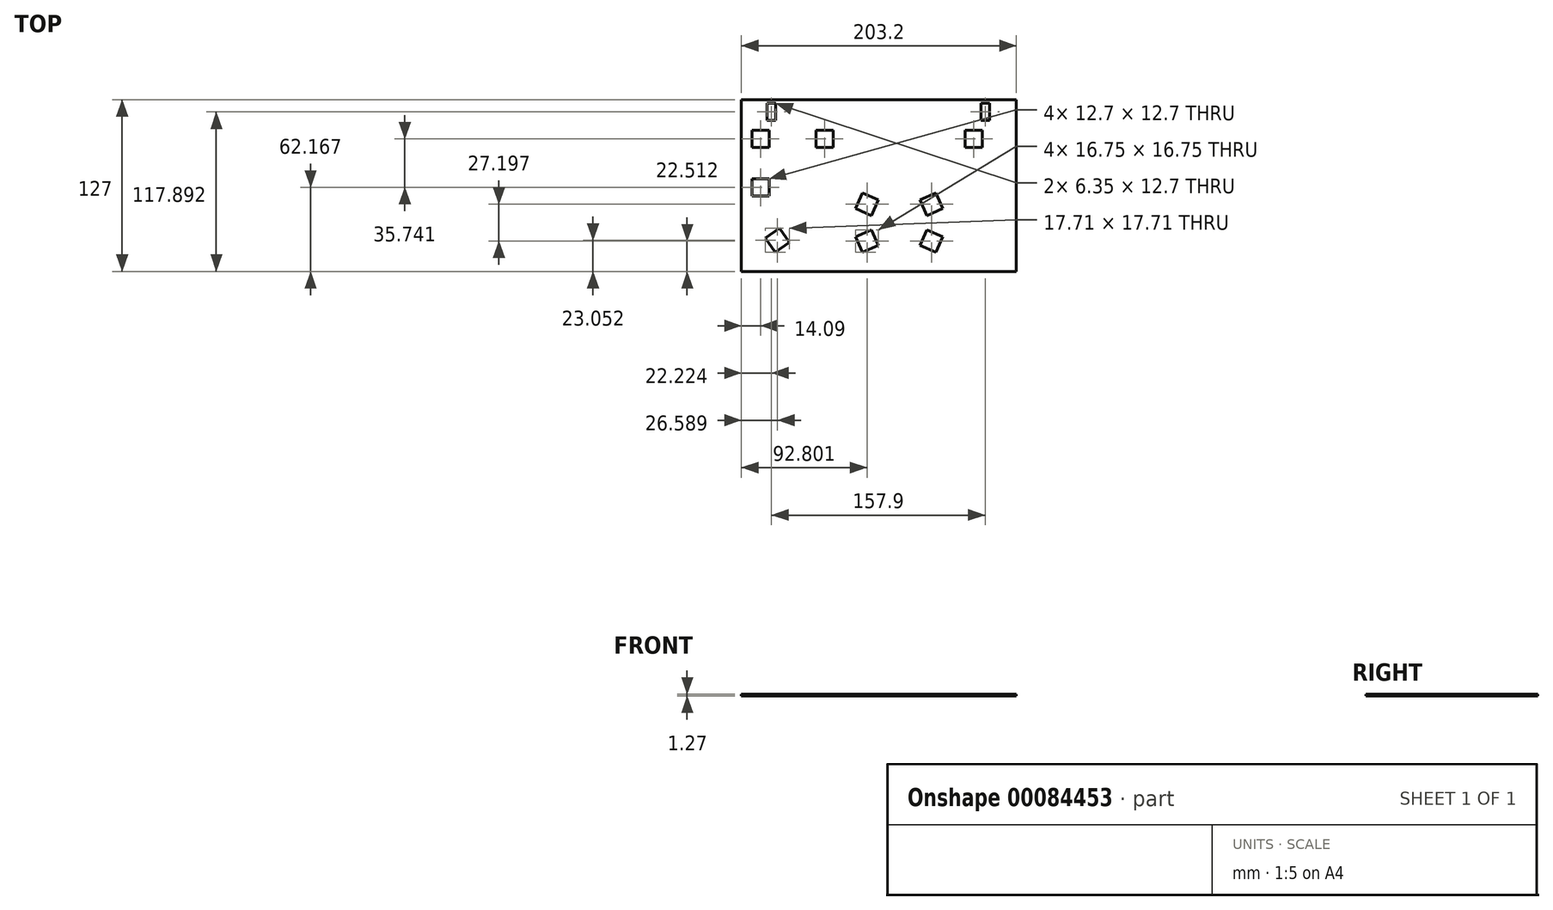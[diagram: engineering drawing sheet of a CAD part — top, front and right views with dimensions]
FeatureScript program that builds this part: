
annotation { "Feature Type Name" : "Feature", "Feature Type Description" : "" }
export const myFeature = defineFeature(function(context is Context, id is Id, definition is map)
    precondition{}
    {
        {
            var Q0;
            Q0=qCreatedBy(makeId("Top.planeOp"),FACE);
            var sketch = newSketch(context, id + "F0", { "sketchPlane" : qUnion([Q0])});
            skLineSegment(sketch, "E0.bottom", {"start": v(-146.8, -36.11) * mm, "end": v(56.4, -36.11) * mm});
            skLineSegment(sketch, "E0.top", {"start": v(-146.8, 90.89) * mm, "end": v(56.4, 90.89) * mm});
            skLineSegment(sketch, "E0.left", {"start": v(-146.8, -36.11) * mm, "end": v(-146.8, 90.89) * mm});
            skLineSegment(sketch, "E0.right", {"start": v(56.4, -36.11) * mm, "end": v(56.4, 90.89) * mm});
            skLineSegment(sketch, "E1.bottom", {"start": v(-139.06, 68.15) * mm, "end": v(-126.36, 68.15) * mm});
            skLineSegment(sketch, "E1.top", {"start": v(-139.06, 55.45) * mm, "end": v(-126.36, 55.45) * mm});
            skLineSegment(sketch, "E1.left", {"start": v(-139.06, 68.15) * mm, "end": v(-139.06, 55.45) * mm});
            skLineSegment(sketch, "E1.right", {"start": v(-126.36, 68.15) * mm, "end": v(-126.36, 55.45) * mm});
            skLineSegment(sketch, "E2.MirrorCS", {"start": v(-139.06, 32.4) * mm, "end": v(-126.36, 32.4) * mm});
            skLineSegment(sketch, "E3.MirrorCS", {"start": v(-139.06, 19.7) * mm, "end": v(-126.36, 19.7) * mm});
            skLineSegment(sketch, "E4.MirrorCS", {"start": v(-126.36, 19.7) * mm, "end": v(-126.36, 32.4) * mm});
            skLineSegment(sketch, "E5.MirrorCS", {"start": v(-139.06, 19.7) * mm, "end": v(-139.06, 32.4) * mm});
            skLineSegment(sketch, "E6.MirrorCS", {"start": v(-129.07, -11.57) * mm, "end": v(-118.72, -4.2) * mm});
            skLineSegment(sketch, "E7.MirrorCS", {"start": v(-118.72, -4.2) * mm, "end": v(-111.36, -14.55) * mm});
            skLineSegment(sketch, "E8.MirrorCS", {"start": v(-129.07, -11.57) * mm, "end": v(-121.7, -21.91) * mm});
            skLineSegment(sketch, "E9.MirrorCS", {"start": v(-121.7, -21.91) * mm, "end": v(-111.36, -14.55) * mm});
            skLineSegment(sketch, "E10.MirrorCS", {"start": v(-79.06, 55.45) * mm, "end": v(-91.76, 55.45) * mm});
            skLineSegment(sketch, "E11.MirrorCS", {"start": v(-91.76, 68.15) * mm, "end": v(-91.76, 55.45) * mm});
            skLineSegment(sketch, "E12.MirrorCS", {"start": v(-79.06, 68.15) * mm, "end": v(-91.76, 68.15) * mm});
            skLineSegment(sketch, "E13.MirrorCS", {"start": v(-79.06, 68.15) * mm, "end": v(-79.06, 55.45) * mm});
            skLineSegment(sketch, "E14.MirrorCS", {"start": v(-45.63, 16.84) * mm, "end": v(-57.24, 21.97) * mm});
            skLineSegment(sketch, "E15.MirrorCS", {"start": v(-45.63, 16.84) * mm, "end": v(-50.76, 5.22) * mm});
            skLineSegment(sketch, "E16.MirrorCS", {"start": v(-50.76, 5.22) * mm, "end": v(-62.37, 10.35) * mm});
            skLineSegment(sketch, "E17.MirrorCS", {"start": v(-57.24, 21.97) * mm, "end": v(-62.37, 10.35) * mm});
            skLineSegment(sketch, "E18.MirrorCS", {"start": v(-45.63, -16.84) * mm, "end": v(-50.76, -5.22) * mm});
            skLineSegment(sketch, "E19.MirrorCS", {"start": v(-57.24, -21.97) * mm, "end": v(-62.37, -10.35) * mm});
            skLineSegment(sketch, "E20.MirrorCS", {"start": v(-50.76, -5.22) * mm, "end": v(-62.37, -10.35) * mm});
            skLineSegment(sketch, "E21.MirrorCS", {"start": v(-45.63, -16.84) * mm, "end": v(-57.24, -21.97) * mm});
            skLineSegment(sketch, "E22.MirrorCS", {"start": v(-14.8, 16.84) * mm, "end": v(-9.67, 5.22) * mm});
            skLineSegment(sketch, "E23.MirrorCS", {"start": v(-9.67, 5.22) * mm, "end": v(1.95, 10.35) * mm});
            skLineSegment(sketch, "E24.MirrorCS", {"start": v(-3.18, 21.97) * mm, "end": v(1.95, 10.35) * mm});
            skLineSegment(sketch, "E25.MirrorCS", {"start": v(-14.8, 16.84) * mm, "end": v(-3.18, 21.97) * mm});
            skLineSegment(sketch, "E26.MirrorCS", {"start": v(-14.8, -16.84) * mm, "end": v(-9.67, -5.22) * mm});
            skLineSegment(sketch, "E27.MirrorCS", {"start": v(-14.8, -16.84) * mm, "end": v(-3.18, -21.97) * mm});
            skLineSegment(sketch, "E28.MirrorCS", {"start": v(-9.67, -5.22) * mm, "end": v(1.95, -10.35) * mm});
            skLineSegment(sketch, "E29.MirrorCS", {"start": v(-3.18, -21.97) * mm, "end": v(1.95, -10.35) * mm});
            skLineSegment(sketch, "E30.MirrorCS", {"start": v(18.63, 68.15) * mm, "end": v(18.63, 55.45) * mm});
            skLineSegment(sketch, "E31.MirrorCS", {"start": v(18.63, 68.15) * mm, "end": v(31.33, 68.15) * mm});
            skLineSegment(sketch, "E32.MirrorCS", {"start": v(31.33, 68.15) * mm, "end": v(31.33, 55.45) * mm});
            skLineSegment(sketch, "E33.MirrorCS", {"start": v(18.63, 55.45) * mm, "end": v(31.33, 55.45) * mm});
            skLineSegment(sketch, "E34.bottom", {"start": v(-127.75, 75.43) * mm, "end": v(-121.4, 75.43) * mm});
            skLineSegment(sketch, "E34.top", {"start": v(-127.75, 88.13) * mm, "end": v(-121.4, 88.13) * mm});
            skLineSegment(sketch, "E34.left", {"start": v(-127.75, 75.43) * mm, "end": v(-127.75, 88.13) * mm});
            skLineSegment(sketch, "E34.right", {"start": v(-121.4, 75.43) * mm, "end": v(-121.4, 88.13) * mm});
            skPoint(sketch, "E35.startSnap0", {"position": v(-45.2, 90.89) * mm});
            skPoint(sketch, "E35.endSnap0", {"position": v(-45.2, -36.11) * mm});
            skLineSegment(sketch, "E36.MirrorCS", {"start": v(36.5, 75.43) * mm, "end": v(36.5, 88.13) * mm});
            skLineSegment(sketch, "E37.MirrorCS", {"start": v(36.5, 88.13) * mm, "end": v(30.15, 88.13) * mm});
            skLineSegment(sketch, "E38.MirrorCS", {"start": v(30.15, 75.43) * mm, "end": v(30.15, 88.13) * mm});
            skLineSegment(sketch, "E39.MirrorCS", {"start": v(36.5, 75.43) * mm, "end": v(30.15, 75.43) * mm});
            skSolve(sketch);
        }
        {
            var Q0;
            Q0=makeQuery(id+"F0.imprint","IMPRINT",FACE,{"disambiguationData":[TD([[makeQuery(id+"F0.imprint","IMPRINT",EDGE,{"derivedFrom":sQuery(id+"F0.wireOp",EDGE,"E0.bottom")}),1.0]])]});
            extrude(context, id + "F1", {"entities" : qUnion([Q0]), "depth" : 1.27 * mm});
        }
    });
